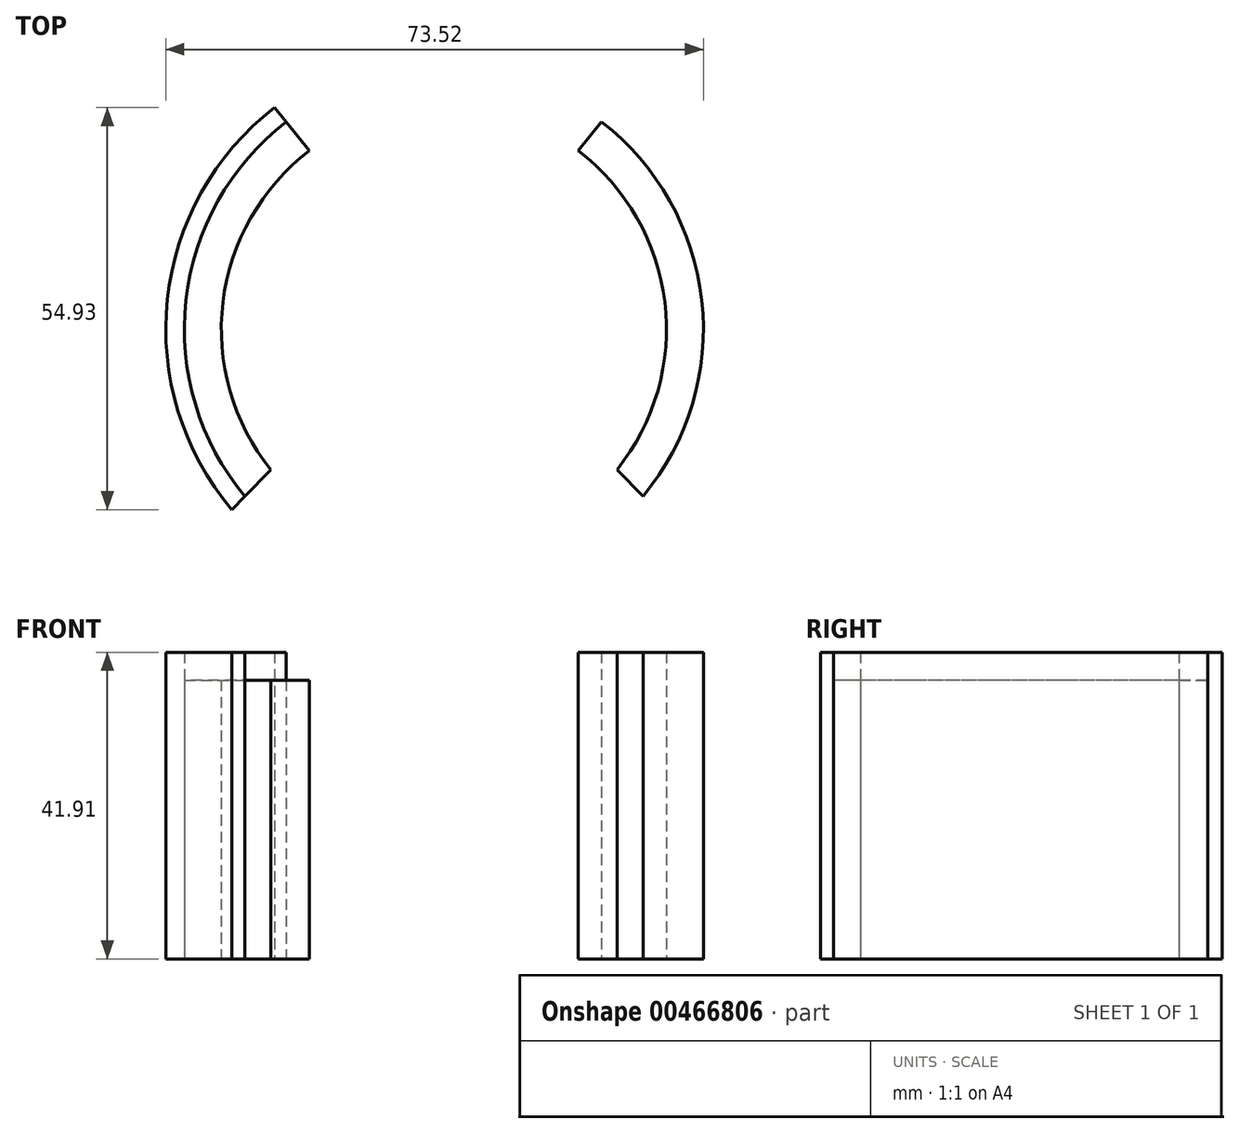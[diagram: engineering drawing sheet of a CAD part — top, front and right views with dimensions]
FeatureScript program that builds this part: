
annotation { "Feature Type Name" : "Feature", "Feature Type Description" : "" }
export const myFeature = defineFeature(function(context is Context, id is Id, definition is map)
    precondition{}
    {
        {
            var Q0;
            Q0=qCreatedBy(makeId("Top.planeOp"),FACE);
            var sketch = newSketch(context, id + "F0", { "sketchPlane" : qUnion([Q0])});
            skCircle(sketch, "E0", {"center": v(0, 0) * mm, "radius": 35.56 * mm});
            skSolve(sketch);
        }
        {
            var Q0;
            Q0=qCreatedBy(makeId("Top.planeOp"),FACE);
            var sketch = newSketch(context, id + "F1", { "sketchPlane" : qUnion([Q0])});
            skArc(sketch, "E1", {"start": v(-18.37, 24.36) * mm, "mid": v(-30.22, 3.68) * mm, "end": v(-23.68, -19.24) * mm});
            skLineSegment(sketch, "E2", {"start": v(-18.37, 24.36) * mm, "end": v(-21.57, 28.27) * mm});
            skLineSegment(sketch, "E3", {"start": v(-23.68, -19.24) * mm, "end": v(-27.23, -22.87) * mm});
            skArc(sketch, "E4", {"start": v(-21.57, 28.27) * mm, "mid": v(-35.27, 3.9) * mm, "end": v(-27.23, -22.87) * mm});
            skLineSegment(sketch, "E5", {"start": v(-21.57, 28.27) * mm, "end": v(-23.17, 30.24) * mm});
            skLineSegment(sketch, "E6", {"start": v(-27.23, -22.87) * mm, "end": v(-29.02, -24.69) * mm});
            skArc(sketch, "E7", {"start": v(-23.17, 30.24) * mm, "mid": v(-37.82, 4.02) * mm, "end": v(-29.02, -24.69) * mm});
            skArc(sketch, "E8.MirrorCS", {"start": v(18.37, 24.36) * mm, "mid": v(30.22, 3.68) * mm, "end": v(23.68, -19.24) * mm});
            skArc(sketch, "E9.MirrorCS", {"start": v(21.57, 28.27) * mm, "mid": v(35.27, 3.9) * mm, "end": v(27.23, -22.87) * mm});
            skArc(sketch, "E10.MirrorCS", {"start": v(23.17, 30.24) * mm, "mid": v(37.82, 4.02) * mm, "end": v(29.02, -24.69) * mm});
            skLineSegment(sketch, "E11.MirrorCS", {"start": v(21.57, 28.27) * mm, "end": v(23.17, 30.24) * mm});
            skLineSegment(sketch, "E12.MirrorCS", {"start": v(18.37, 24.36) * mm, "end": v(21.57, 28.27) * mm});
            skLineSegment(sketch, "E13.MirrorCS", {"start": v(23.68, -19.24) * mm, "end": v(27.23, -22.87) * mm});
            skLineSegment(sketch, "E14.MirrorCS", {"start": v(27.23, -22.87) * mm, "end": v(29.02, -24.69) * mm});
            skSolve(sketch);
        }
        {
            var Q0;
            Q0=makeQuery(id+"F1.imprint","IMPRINT",FACE,{"disambiguationData":[TD([[makeQuery(id+"F1.imprint","IMPRINT",EDGE,{"derivedFrom":sQuery(id+"F1.wireOp",EDGE,"E4")}),-1.0]])]});
            var Q1;
            Q1=makeQuery(id+"F1.imprint","IMPRINT",FACE,{"disambiguationData":[TD([[makeQuery(id+"F1.imprint","IMPRINT",EDGE,{"derivedFrom":sQuery(id+"F1.wireOp",EDGE,"E9.MirrorCS")}),1.0]])]});
            extrude(context, id + "F2", {"entities" : qUnion([Q0, Q1]), "depth" : 41.9 * mm});
        }
        {
            var Q0;
            Q0=makeQuery(id+"F1.imprint","IMPRINT",FACE,{"disambiguationData":[TD([[makeQuery(id+"F1.imprint","IMPRINT",EDGE,{"derivedFrom":sQuery(id+"F1.wireOp",EDGE,"E1")}),-1.0]])]});
            var Q1;
            Q1=makeQuery(id+"F1.imprint","IMPRINT",FACE,{"disambiguationData":[TD([[makeQuery(id+"F1.imprint","IMPRINT",EDGE,{"derivedFrom":sQuery(id+"F1.wireOp",EDGE,"E8.MirrorCS")}),1.0]])]});
            extrude(context, id + "F3", {"entities" : qUnion([Q0, Q1]), "depth" : 38.1 * mm});
        }
    });
